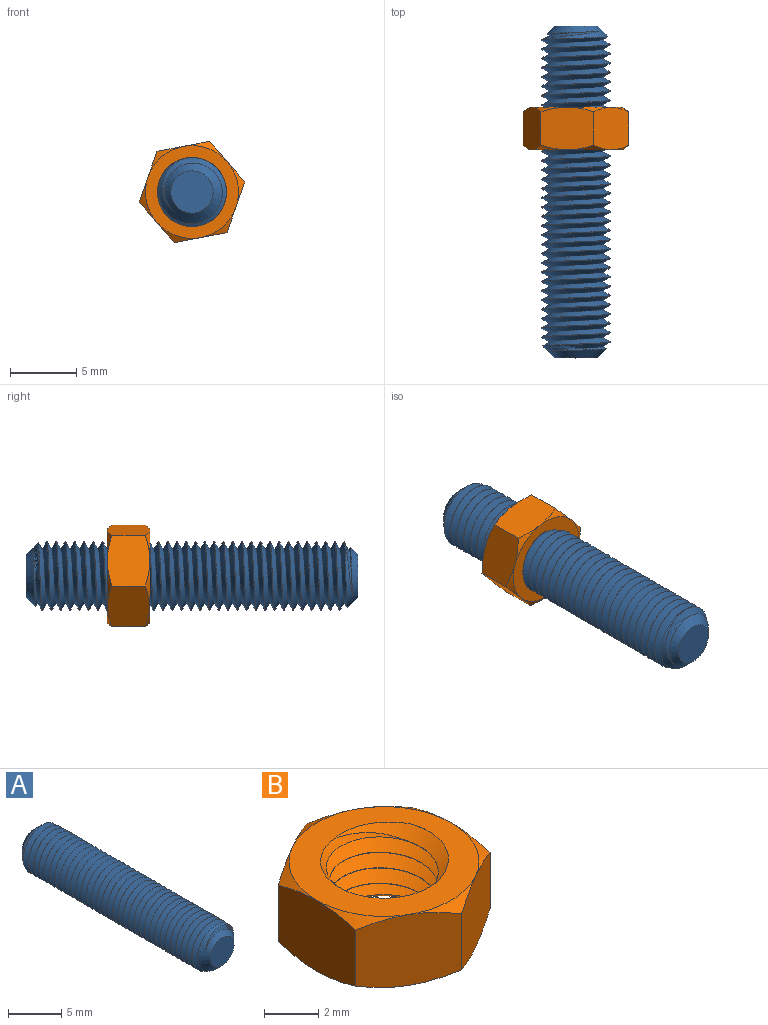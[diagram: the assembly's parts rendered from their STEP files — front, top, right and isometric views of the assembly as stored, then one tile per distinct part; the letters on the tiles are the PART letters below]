
ASSEMBLY  parts=2 mates=1
PART A: 8 faces, bbox 5.2x25x6 mm
  f0: cylinder r=2.59mm len=23mm, axis (0,1,0), area 13.9mm2, adj f4,f5,f6,f7
  f1: plane 3.19x3.19mm, normal (0,-1,0), area 8mm2, adj f3
  f2: plane 3.19x3.19mm, normal (0,1,0), area 8mm2, adj f5
  f3: cone r=1.59mm half-angle=45deg, axis (0,1,0), area 12.4mm2, adj f1,f4,f6,f7
  f4: cone r=1.59mm half-angle=45deg, axis (0,1,0), area 0mm2, adj f0,f3,f7
  f5: cone r=2.59mm half-angle=45deg, axis (0,-1,0), area 12.4mm2, adj f0,f2,f6,f7
  f6: bspline ~24.61x5.99mm, area 332.9mm2, adj f0,f3,f5,f7
  f7: bspline ~24.61x5.99mm, area 332.3mm2, adj f0,f3,f4,f5,f6
PART B: 25 faces, bbox 8.4x8.4x4.4 mm
  f0: plane 7.1x7.1mm, normal (0,0,1), area 20.5mm2, adj f5,f6,f8,f10,f12,f14,f22,f23
  f1: plane 7.12x7.12mm, normal (0,0,-1), area 20.5mm2, adj f3,f4,f7,f9,f11,f13,f21,f23
  f2: cylinder r=2mm len=4mm, axis (0,0,-1), area 1mm2, adj f21,f22,f23,f24
  f3: cone r=3.5mm half-angle=58.3deg, axis (0,0,1), area 1.2mm2, adj f1,f15,f16
  f4: cone r=3.5mm half-angle=58.3deg, axis (0,0,1), area 1.2mm2, adj f1,f15,f20
  f5: cone r=3.5mm half-angle=58.3deg, axis (0,0,-1), area 1.2mm2, adj f0,f15,f16
  f6: cone r=3.5mm half-angle=58.3deg, axis (0,0,-1), area 1.2mm2, adj f0,f15,f20
  f7: cone r=3.5mm half-angle=58.3deg, axis (0,0,1), area 1.2mm2, adj f1,f16,f17
  f8: cone r=3.5mm half-angle=58.3deg, axis (0,0,-1), area 1.2mm2, adj f0,f16,f17
  f9: cone r=3.5mm half-angle=58.3deg, axis (0,0,1), area 1.2mm2, adj f1,f17,f18
  f10: cone r=3.5mm half-angle=58.3deg, axis (0,0,-1), area 1.2mm2, adj f0,f17,f18
  f11: cone r=3.5mm half-angle=58.3deg, axis (0,0,1), area 1.2mm2, adj f1,f18,f19
  f12: cone r=3.5mm half-angle=58.3deg, axis (0,0,-1), area 1.2mm2, adj f0,f18,f19
  f13: cone r=3.5mm half-angle=58.3deg, axis (0,0,1), area 1.2mm2, adj f1,f19,f20
  f14: cone r=3.5mm half-angle=58.3deg, axis (0,0,-1), area 1.2mm2, adj f0,f19,f20
  f15: plane 4.38x3.54mm, normal (1,0,0), area 12mm2, adj f3,f4,f5,f6,f16,f20
  f16: plane 3.84x3.54mm, normal (0.5,-0.87,0), area 12mm2, adj f3,f5,f7,f8,f15,f17
  f17: plane 3.84x3.54mm, normal (-0.5,-0.87,0), area 12mm2, adj f7,f8,f9,f10,f16,f18
  f18: plane 4.38x3.54mm, normal (-1,0,0), area 12mm2, adj f9,f10,f11,f12,f17,f19
  f19: plane 3.84x3.54mm, normal (-0.5,0.87,0), area 12mm2, adj f11,f12,f13,f14,f18,f20
  f20: plane 3.84x3.54mm, normal (0.5,0.87,0), area 12mm2, adj f4,f6,f13,f14,f15,f19
  f21: cone r=2.34mm half-angle=45deg, axis (0,0,-1), area 2mm2, adj f1,f2,f23,f24
  f22: cone r=2mm half-angle=45deg, axis (0,0,1), area 2mm2, adj f0,f2,f23,f24
  f23: bspline ~5.99x5.19mm, area 42.8mm2, adj f0,f1,f2,f21,f22,f24
  f24: bspline ~5.99x5.19mm, area 42.8mm2, adj f0,f1,f2,f21,f22,f23
PLACE A rot(axis=(0,-1,0),76.1deg) t=(-6.31,9.2,-19.64)mm fixed
PLACE B rot(axis=(0.51,-0.61,0.61),126.4deg) t=(-6.31,3.08,-19.64)mm
MATE cylindrical A.f0 <-> B.f3  axis (0,1,0) through (-6.31,9.2,-19.64)mm
